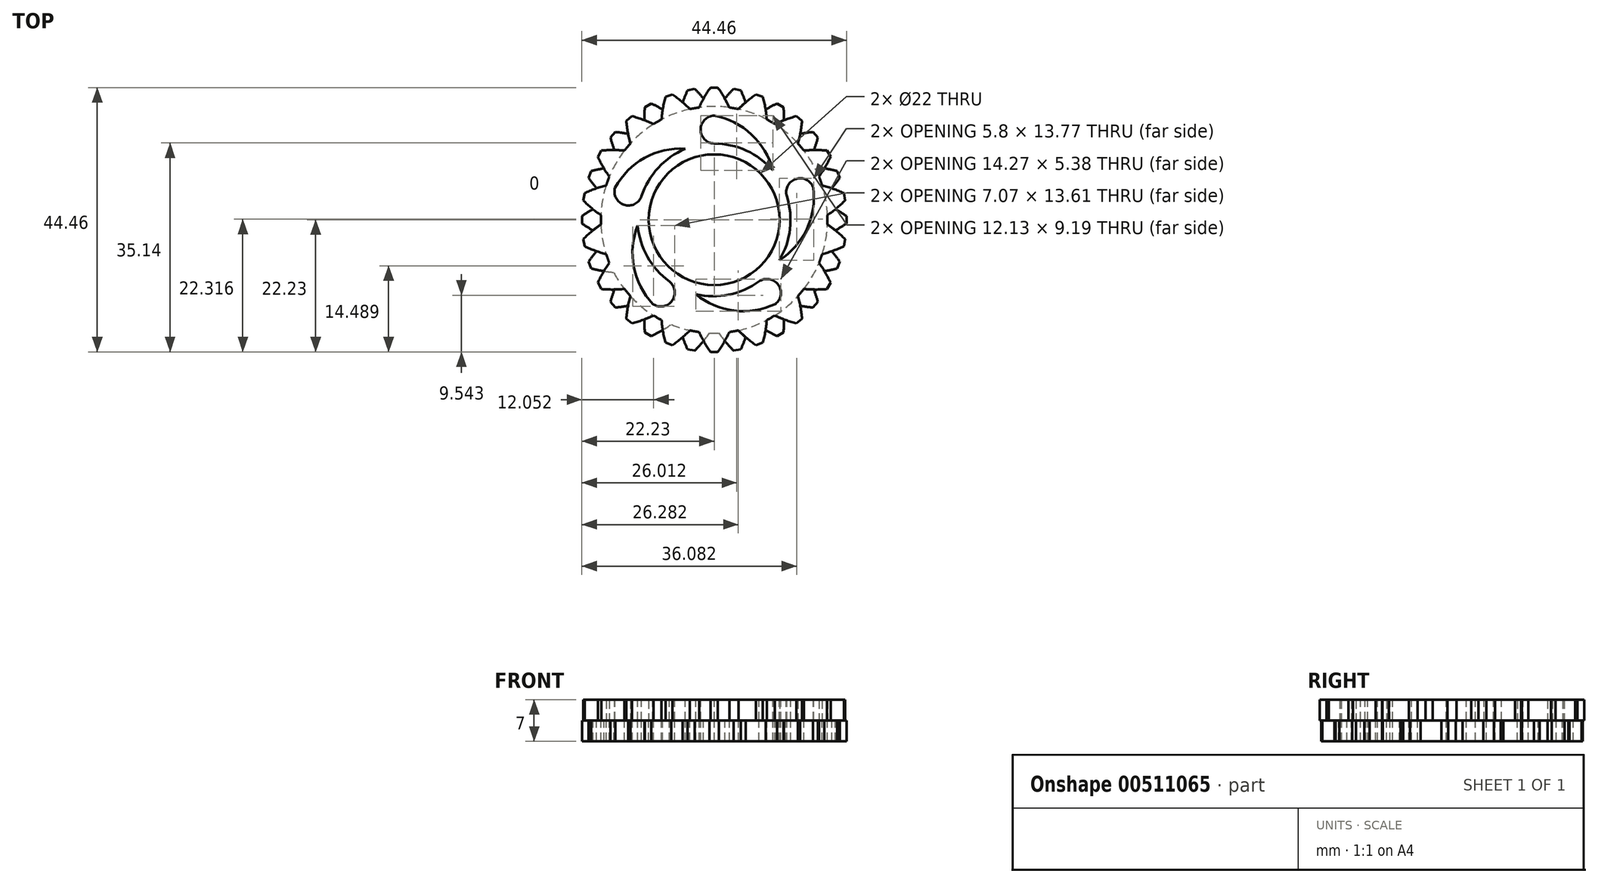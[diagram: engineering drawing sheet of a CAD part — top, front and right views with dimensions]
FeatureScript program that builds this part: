
annotation { "Feature Type Name" : "Feature", "Feature Type Description" : "" }
export const myFeature = defineFeature(function(context is Context, id is Id, definition is map)
    precondition{}
    {
        {
            var Q0;
            Q0=qCreatedBy(makeId("Top.planeOp"),FACE);
            var sketch = newSketch(context, id + "F0", { "sketchPlane" : qUnion([Q0])});
            skCircle(sketch, "E0", {"center": v(0, 0) * mm, "radius": 19.05 * mm});
            skCircle(sketch, "E1", {"center": v(0, 0) * mm, "radius": 11 * mm});
            skLineSegment(sketch, "E2", {"start": v(-2.54, 18.88) * mm, "end": v(-1, 22.23) * mm});
            skLineSegment(sketch, "E3", {"start": v(-1, 22.23) * mm, "end": v(1, 22.23) * mm});
            skLineSegment(sketch, "E4", {"start": v(1, 22.23) * mm, "end": v(2.54, 18.88) * mm});
            skArc(sketch, "E5", {"start": v(-0.62, 22.23) * mm, "mid": v(-1.65, 20.6) * mm, "end": v(-2.54, 18.88) * mm});
            skArc(sketch, "E6", {"start": v(2.54, 18.88) * mm, "mid": v(1.65, 20.6) * mm, "end": v(0.62, 22.23) * mm});
            skArc(sketch, "E7.1.0", {"start": v(-8.18, 20.67) * mm, "mid": v(-8.6, 18.79) * mm, "end": v(-8.84, 16.87) * mm});
            skLineSegment(sketch, "E7.1.1", {"start": v(-8.54, 20.54) * mm, "end": v(-6.66, 21.23) * mm});
            skArc(sketch, "E7.1.2", {"start": v(-4.07, 18.61) * mm, "mid": v(-5.49, 19.92) * mm, "end": v(-7.02, 21.1) * mm});
            skArc(sketch, "E7.2.0", {"start": v(-14.76, 16.63) * mm, "mid": v(-14.5, 14.71) * mm, "end": v(-14.08, 12.83) * mm});
            skLineSegment(sketch, "E7.2.1", {"start": v(-15.05, 16.38) * mm, "end": v(-13.52, 17.67) * mm});
            skArc(sketch, "E7.2.2", {"start": v(-10.2, 16.1) * mm, "mid": v(-11.97, 16.84) * mm, "end": v(-13.81, 17.42) * mm});
            skArc(sketch, "E7.3.0", {"start": v(-19.56, 10.58) * mm, "mid": v(-18.66, 8.86) * mm, "end": v(-17.62, 7.24) * mm});
            skLineSegment(sketch, "E7.3.1", {"start": v(-19.75, 10.25) * mm, "end": v(-18.75, 11.98) * mm});
            skArc(sketch, "E7.3.2", {"start": v(-15.08, 11.64) * mm, "mid": v(-17, 11.73) * mm, "end": v(-18.94, 11.65) * mm});
            skArc(sketch, "E7.4.0", {"start": v(-22, 3.25) * mm, "mid": v(-20.57, 1.95) * mm, "end": v(-19.03, 0.78) * mm});
            skLineSegment(sketch, "E7.4.1", {"start": v(-22.06, 2.87) * mm, "end": v(-21.71, 4.84) * mm});
            skArc(sketch, "E7.4.2", {"start": v(-18.15, 5.78) * mm, "mid": v(-20, 5.2) * mm, "end": v(-21.78, 4.47) * mm});
            skArc(sketch, "E7.5.0", {"start": v(-21.78, -4.47) * mm, "mid": v(-20, -5.2) * mm, "end": v(-18.15, -5.78) * mm});
            skLineSegment(sketch, "E7.5.1", {"start": v(-21.71, -4.84) * mm, "end": v(-22.06, -2.87) * mm});
            skArc(sketch, "E7.5.2", {"start": v(-19.03, -0.78) * mm, "mid": v(-20.57, -1.95) * mm, "end": v(-22, -3.25) * mm});
            skArc(sketch, "E7.6.0", {"start": v(-18.94, -11.65) * mm, "mid": v(-17, -11.73) * mm, "end": v(-15.08, -11.64) * mm});
            skLineSegment(sketch, "E7.6.1", {"start": v(-18.75, -11.98) * mm, "end": v(-19.75, -10.25) * mm});
            skArc(sketch, "E7.6.2", {"start": v(-17.62, -7.24) * mm, "mid": v(-18.66, -8.86) * mm, "end": v(-19.56, -10.58) * mm});
            skArc(sketch, "E7.7.0", {"start": v(-13.81, -17.42) * mm, "mid": v(-11.97, -16.84) * mm, "end": v(-10.2, -16.1) * mm});
            skLineSegment(sketch, "E7.7.1", {"start": v(-13.52, -17.67) * mm, "end": v(-15.05, -16.38) * mm});
            skArc(sketch, "E7.7.2", {"start": v(-14.08, -12.83) * mm, "mid": v(-14.5, -14.71) * mm, "end": v(-14.76, -16.63) * mm});
            skArc(sketch, "E7.8.0", {"start": v(-7.02, -21.1) * mm, "mid": v(-5.49, -19.92) * mm, "end": v(-4.07, -18.61) * mm});
            skLineSegment(sketch, "E7.8.1", {"start": v(-6.66, -21.23) * mm, "end": v(-8.54, -20.54) * mm});
            skArc(sketch, "E7.8.2", {"start": v(-8.84, -16.87) * mm, "mid": v(-8.6, -18.79) * mm, "end": v(-8.18, -20.67) * mm});
            skArc(sketch, "E7.9.0", {"start": v(0.62, -22.23) * mm, "mid": v(1.65, -20.6) * mm, "end": v(2.54, -18.88) * mm});
            skLineSegment(sketch, "E7.9.1", {"start": v(1, -22.23) * mm, "end": v(-1, -22.23) * mm});
            skArc(sketch, "E7.9.2", {"start": v(-2.54, -18.88) * mm, "mid": v(-1.65, -20.6) * mm, "end": v(-0.62, -22.23) * mm});
            skArc(sketch, "E7.10.0", {"start": v(8.18, -20.67) * mm, "mid": v(8.6, -18.79) * mm, "end": v(8.84, -16.87) * mm});
            skLineSegment(sketch, "E7.10.1", {"start": v(8.54, -20.54) * mm, "end": v(6.66, -21.23) * mm});
            skArc(sketch, "E7.10.2", {"start": v(4.07, -18.61) * mm, "mid": v(5.49, -19.92) * mm, "end": v(7.02, -21.1) * mm});
            skArc(sketch, "E7.11.0", {"start": v(14.76, -16.63) * mm, "mid": v(14.5, -14.71) * mm, "end": v(14.08, -12.83) * mm});
            skLineSegment(sketch, "E7.11.1", {"start": v(15.05, -16.38) * mm, "end": v(13.52, -17.67) * mm});
            skArc(sketch, "E7.11.2", {"start": v(10.2, -16.1) * mm, "mid": v(11.97, -16.84) * mm, "end": v(13.81, -17.42) * mm});
            skArc(sketch, "E7.12.0", {"start": v(19.56, -10.58) * mm, "mid": v(18.66, -8.86) * mm, "end": v(17.62, -7.24) * mm});
            skLineSegment(sketch, "E7.12.1", {"start": v(19.75, -10.25) * mm, "end": v(18.75, -11.98) * mm});
            skArc(sketch, "E7.12.2", {"start": v(15.08, -11.64) * mm, "mid": v(17, -11.73) * mm, "end": v(18.94, -11.65) * mm});
            skArc(sketch, "E7.13.0", {"start": v(22, -3.25) * mm, "mid": v(20.57, -1.95) * mm, "end": v(19.03, -0.78) * mm});
            skLineSegment(sketch, "E7.13.1", {"start": v(22.06, -2.87) * mm, "end": v(21.71, -4.84) * mm});
            skArc(sketch, "E7.13.2", {"start": v(18.15, -5.78) * mm, "mid": v(20, -5.2) * mm, "end": v(21.78, -4.47) * mm});
            skArc(sketch, "E7.14.0", {"start": v(21.78, 4.47) * mm, "mid": v(20, 5.2) * mm, "end": v(18.15, 5.78) * mm});
            skLineSegment(sketch, "E7.14.1", {"start": v(21.71, 4.84) * mm, "end": v(22.06, 2.87) * mm});
            skArc(sketch, "E7.14.2", {"start": v(19.03, 0.78) * mm, "mid": v(20.57, 1.95) * mm, "end": v(22, 3.25) * mm});
            skArc(sketch, "E7.15.0", {"start": v(18.94, 11.65) * mm, "mid": v(17, 11.73) * mm, "end": v(15.08, 11.64) * mm});
            skLineSegment(sketch, "E7.15.1", {"start": v(18.75, 11.98) * mm, "end": v(19.75, 10.25) * mm});
            skArc(sketch, "E7.15.2", {"start": v(17.62, 7.24) * mm, "mid": v(18.66, 8.86) * mm, "end": v(19.56, 10.58) * mm});
            skArc(sketch, "E7.16.0", {"start": v(13.81, 17.42) * mm, "mid": v(11.97, 16.84) * mm, "end": v(10.2, 16.1) * mm});
            skLineSegment(sketch, "E7.16.1", {"start": v(13.52, 17.67) * mm, "end": v(15.05, 16.38) * mm});
            skArc(sketch, "E7.16.2", {"start": v(14.08, 12.83) * mm, "mid": v(14.5, 14.71) * mm, "end": v(14.76, 16.63) * mm});
            skArc(sketch, "E7.17.0", {"start": v(7.02, 21.1) * mm, "mid": v(5.49, 19.92) * mm, "end": v(4.07, 18.61) * mm});
            skLineSegment(sketch, "E7.17.1", {"start": v(6.66, 21.23) * mm, "end": v(8.54, 20.54) * mm});
            skArc(sketch, "E7.17.2", {"start": v(8.84, 16.87) * mm, "mid": v(8.6, 18.79) * mm, "end": v(8.18, 20.67) * mm});
            skSolve(sketch);
        }
        {
            var Q0;
            {var subQ0=sQuery(id+"F0.wireOp",EDGE,"E7.1.0");Q0=makeQuery(id+"F0.imprint","IMPRINT",FACE,{"disambiguationData":[TD([[makeQuery(id+"F0.imprint","IMPRINT",EDGE,{"derivedFrom":subQ0}),1.0]])]});}
            var Q1;
            Q1=makeQuery(id+"F0.imprint","IMPRINT",FACE,{"disambiguationData":[TD([[makeQuery(id+"F0.imprint","IMPRINT",EDGE,{"derivedFrom":sQuery(id+"F0.wireOp",EDGE,"E1")}),-1.0]])]});
            var Q2;
            {var subQ0=sQuery(id+"F0.wireOp",EDGE,"E5");Q2=makeQuery(id+"F0.imprint","IMPRINT",FACE,{"disambiguationData":[TD([[makeQuery(id+"F0.imprint","IMPRINT",EDGE,{"derivedFrom":subQ0}),1.0]])]});}
            var Q3;
            {var subQ0=sQuery(id+"F0.wireOp",EDGE,"E7.17.0");Q3=makeQuery(id+"F0.imprint","IMPRINT",FACE,{"disambiguationData":[TD([[makeQuery(id+"F0.imprint","IMPRINT",EDGE,{"derivedFrom":subQ0}),1.0]])]});}
            var Q4;
            {var subQ0=sQuery(id+"F0.wireOp",EDGE,"E7.16.0");Q4=makeQuery(id+"F0.imprint","IMPRINT",FACE,{"disambiguationData":[TD([[makeQuery(id+"F0.imprint","IMPRINT",EDGE,{"derivedFrom":subQ0}),1.0]])]});}
            var Q5;
            {var subQ0=sQuery(id+"F0.wireOp",EDGE,"E7.15.0");Q5=makeQuery(id+"F0.imprint","IMPRINT",FACE,{"disambiguationData":[TD([[makeQuery(id+"F0.imprint","IMPRINT",EDGE,{"derivedFrom":subQ0}),1.0]])]});}
            var Q6;
            {var subQ0=sQuery(id+"F0.wireOp",EDGE,"E7.14.0");Q6=makeQuery(id+"F0.imprint","IMPRINT",FACE,{"disambiguationData":[TD([[makeQuery(id+"F0.imprint","IMPRINT",EDGE,{"derivedFrom":subQ0}),1.0]])]});}
            var Q7;
            {var subQ0=sQuery(id+"F0.wireOp",EDGE,"E7.13.0");Q7=makeQuery(id+"F0.imprint","IMPRINT",FACE,{"disambiguationData":[TD([[makeQuery(id+"F0.imprint","IMPRINT",EDGE,{"derivedFrom":subQ0}),1.0]])]});}
            var Q8;
            {var subQ0=sQuery(id+"F0.wireOp",EDGE,"E7.12.0");Q8=makeQuery(id+"F0.imprint","IMPRINT",FACE,{"disambiguationData":[TD([[makeQuery(id+"F0.imprint","IMPRINT",EDGE,{"derivedFrom":subQ0}),1.0]])]});}
            var Q9;
            {var subQ0=sQuery(id+"F0.wireOp",EDGE,"E7.11.0");Q9=makeQuery(id+"F0.imprint","IMPRINT",FACE,{"disambiguationData":[TD([[makeQuery(id+"F0.imprint","IMPRINT",EDGE,{"derivedFrom":subQ0}),1.0]])]});}
            var Q10;
            {var subQ0=sQuery(id+"F0.wireOp",EDGE,"E7.10.0");Q10=makeQuery(id+"F0.imprint","IMPRINT",FACE,{"disambiguationData":[TD([[makeQuery(id+"F0.imprint","IMPRINT",EDGE,{"derivedFrom":subQ0}),1.0]])]});}
            var Q11;
            {var subQ0=sQuery(id+"F0.wireOp",EDGE,"E7.9.0");Q11=makeQuery(id+"F0.imprint","IMPRINT",FACE,{"disambiguationData":[TD([[makeQuery(id+"F0.imprint","IMPRINT",EDGE,{"derivedFrom":subQ0}),1.0]])]});}
            var Q12;
            {var subQ0=sQuery(id+"F0.wireOp",EDGE,"E7.8.0");Q12=makeQuery(id+"F0.imprint","IMPRINT",FACE,{"disambiguationData":[TD([[makeQuery(id+"F0.imprint","IMPRINT",EDGE,{"derivedFrom":subQ0}),1.0]])]});}
            var Q13;
            {var subQ0=sQuery(id+"F0.wireOp",EDGE,"E7.7.0");Q13=makeQuery(id+"F0.imprint","IMPRINT",FACE,{"disambiguationData":[TD([[makeQuery(id+"F0.imprint","IMPRINT",EDGE,{"derivedFrom":subQ0}),1.0]])]});}
            var Q14;
            {var subQ0=sQuery(id+"F0.wireOp",EDGE,"E7.6.0");Q14=makeQuery(id+"F0.imprint","IMPRINT",FACE,{"disambiguationData":[TD([[makeQuery(id+"F0.imprint","IMPRINT",EDGE,{"derivedFrom":subQ0}),1.0]])]});}
            var Q15;
            {var subQ0=sQuery(id+"F0.wireOp",EDGE,"E7.5.0");Q15=makeQuery(id+"F0.imprint","IMPRINT",FACE,{"disambiguationData":[TD([[makeQuery(id+"F0.imprint","IMPRINT",EDGE,{"derivedFrom":subQ0}),1.0]])]});}
            var Q16;
            {var subQ0=sQuery(id+"F0.wireOp",EDGE,"E7.4.0");Q16=makeQuery(id+"F0.imprint","IMPRINT",FACE,{"disambiguationData":[TD([[makeQuery(id+"F0.imprint","IMPRINT",EDGE,{"derivedFrom":subQ0}),1.0]])]});}
            var Q17;
            {var subQ0=sQuery(id+"F0.wireOp",EDGE,"E7.3.0");Q17=makeQuery(id+"F0.imprint","IMPRINT",FACE,{"disambiguationData":[TD([[makeQuery(id+"F0.imprint","IMPRINT",EDGE,{"derivedFrom":subQ0}),1.0]])]});}
            var Q18;
            {var subQ0=sQuery(id+"F0.wireOp",EDGE,"E7.2.0");Q18=makeQuery(id+"F0.imprint","IMPRINT",FACE,{"disambiguationData":[TD([[makeQuery(id+"F0.imprint","IMPRINT",EDGE,{"derivedFrom":subQ0}),1.0]])]});}
            extrude(context, id + "F1", {"entities" : qUnion([Q0, Q1, Q2, Q3, Q4, Q5, Q6, Q7, Q8, Q9, Q10, Q11, Q12, Q13, Q14, Q15, Q16, Q17, Q18]), "depth" : 3.5 * mm, "offsetDistance" : 25.4 * mm});
        }
        {
            var Q0;
            Q0=makeQuery(id+"F1.opExtrude","CAP_FACE",FACE,{"disambiguationData":[OSD([sQuery(id+"F0.wireOp",EDGE,"E0"),sQuery(id+"F0.wireOp",EDGE,"E1"),sQuery(id+"F0.wireOp",EDGE,"E3"),sQuery(id+"F0.wireOp",EDGE,"E5"),sQuery(id+"F0.wireOp",EDGE,"E6"),sQuery(id+"F0.wireOp",EDGE,"E7.1.0"),sQuery(id+"F0.wireOp",EDGE,"E7.1.1"),sQuery(id+"F0.wireOp",EDGE,"E7.1.2"),sQuery(id+"F0.wireOp",EDGE,"E7.2.0"),sQuery(id+"F0.wireOp",EDGE,"E7.2.1"),sQuery(id+"F0.wireOp",EDGE,"E7.2.2"),sQuery(id+"F0.wireOp",EDGE,"E7.3.0"),sQuery(id+"F0.wireOp",EDGE,"E7.3.1"),sQuery(id+"F0.wireOp",EDGE,"E7.3.2"),sQuery(id+"F0.wireOp",EDGE,"E7.4.0"),sQuery(id+"F0.wireOp",EDGE,"E7.4.1"),sQuery(id+"F0.wireOp",EDGE,"E7.4.2"),sQuery(id+"F0.wireOp",EDGE,"E7.5.0"),sQuery(id+"F0.wireOp",EDGE,"E7.5.1"),sQuery(id+"F0.wireOp",EDGE,"E7.5.2"),sQuery(id+"F0.wireOp",EDGE,"E7.6.0"),sQuery(id+"F0.wireOp",EDGE,"E7.6.1"),sQuery(id+"F0.wireOp",EDGE,"E7.6.2"),sQuery(id+"F0.wireOp",EDGE,"E7.7.0"),sQuery(id+"F0.wireOp",EDGE,"E7.7.1"),sQuery(id+"F0.wireOp",EDGE,"E7.7.2"),sQuery(id+"F0.wireOp",EDGE,"E7.8.0"),sQuery(id+"F0.wireOp",EDGE,"E7.8.1"),sQuery(id+"F0.wireOp",EDGE,"E7.8.2"),sQuery(id+"F0.wireOp",EDGE,"E7.9.0"),sQuery(id+"F0.wireOp",EDGE,"E7.9.1"),sQuery(id+"F0.wireOp",EDGE,"E7.9.2"),sQuery(id+"F0.wireOp",EDGE,"E7.10.0"),sQuery(id+"F0.wireOp",EDGE,"E7.10.1"),sQuery(id+"F0.wireOp",EDGE,"E7.10.2"),sQuery(id+"F0.wireOp",EDGE,"E7.11.0"),sQuery(id+"F0.wireOp",EDGE,"E7.11.1"),sQuery(id+"F0.wireOp",EDGE,"E7.11.2"),sQuery(id+"F0.wireOp",EDGE,"E7.12.0"),sQuery(id+"F0.wireOp",EDGE,"E7.12.1"),sQuery(id+"F0.wireOp",EDGE,"E7.12.2"),sQuery(id+"F0.wireOp",EDGE,"E7.13.0"),sQuery(id+"F0.wireOp",EDGE,"E7.13.1"),sQuery(id+"F0.wireOp",EDGE,"E7.13.2"),sQuery(id+"F0.wireOp",EDGE,"E7.14.0"),sQuery(id+"F0.wireOp",EDGE,"E7.14.1"),sQuery(id+"F0.wireOp",EDGE,"E7.14.2"),sQuery(id+"F0.wireOp",EDGE,"E7.15.0"),sQuery(id+"F0.wireOp",EDGE,"E7.15.1"),sQuery(id+"F0.wireOp",EDGE,"E7.15.2"),sQuery(id+"F0.wireOp",EDGE,"E7.16.0"),sQuery(id+"F0.wireOp",EDGE,"E7.16.1"),sQuery(id+"F0.wireOp",EDGE,"E7.16.2"),sQuery(id+"F0.wireOp",EDGE,"E7.17.0"),sQuery(id+"F0.wireOp",EDGE,"E7.17.1"),sQuery(id+"F0.wireOp",EDGE,"E7.17.2")])],"isStart":true});
            var sketch = newSketch(context, id + "F2", { "sketchPlane" : qUnion([Q0])});
            skCircle(sketch, "E8.0", {"center": v(0, 0) * mm, "radius": 11 * mm});
            skArc(sketch, "E9.0", {"start": v(-2.54, 18.88) * mm, "mid": v(-1.65, 20.6) * mm, "end": v(-0.62, 22.23) * mm});
            skLineSegment(sketch, "E10.0", {"start": v(0.62, 22.23) * mm, "end": v(-0.62, 22.23) * mm});
            skArc(sketch, "E11.0", {"start": v(0.62, 22.23) * mm, "mid": v(1.65, 20.6) * mm, "end": v(2.54, 18.88) * mm});
            skArc(sketch, "E12.1.0", {"start": v(-5.78, 18.15) * mm, "mid": v(-5.2, 20) * mm, "end": v(-4.47, 21.78) * mm});
            skLineSegment(sketch, "E12.1.1", {"start": v(-3.25, 22) * mm, "end": v(-4.47, 21.78) * mm});
            skArc(sketch, "E12.1.2", {"start": v(-3.25, 22) * mm, "mid": v(-1.95, 20.57) * mm, "end": v(-0.78, 19.03) * mm});
            skArc(sketch, "E12.2.0", {"start": v(-8.84, 16.87) * mm, "mid": v(-8.6, 18.79) * mm, "end": v(-8.18, 20.67) * mm});
            skArc(sketch, "E12.3.0", {"start": v(-11.64, 15.08) * mm, "mid": v(-11.73, 17) * mm, "end": v(-11.65, 18.94) * mm});
            skLineSegment(sketch, "E12.3.1", {"start": v(-10.58, 19.56) * mm, "end": v(-11.65, 18.94) * mm});
            skArc(sketch, "E12.3.2", {"start": v(-10.58, 19.56) * mm, "mid": v(-8.86, 18.66) * mm, "end": v(-7.24, 17.62) * mm});
            skArc(sketch, "E12.5.0", {"start": v(-16.1, 10.2) * mm, "mid": v(-16.84, 11.97) * mm, "end": v(-17.42, 13.81) * mm});
            skLineSegment(sketch, "E12.5.1", {"start": v(-16.63, 14.76) * mm, "end": v(-17.42, 13.81) * mm});
            skArc(sketch, "E12.5.2", {"start": v(-16.63, 14.76) * mm, "mid": v(-14.71, 14.5) * mm, "end": v(-12.83, 14.08) * mm});
            skArc(sketch, "E12.6.0", {"start": v(-17.62, 7.24) * mm, "mid": v(-18.66, 8.86) * mm, "end": v(-19.56, 10.58) * mm});
            skLineSegment(sketch, "E12.6.1", {"start": v(-18.94, 11.65) * mm, "end": v(-19.56, 10.58) * mm});
            skArc(sketch, "E12.6.2", {"start": v(-18.94, 11.65) * mm, "mid": v(-17, 11.73) * mm, "end": v(-15.08, 11.64) * mm});
            skArc(sketch, "E12.7.0", {"start": v(-18.61, 4.07) * mm, "mid": v(-19.92, 5.49) * mm, "end": v(-21.1, 7.02) * mm});
            skLineSegment(sketch, "E12.7.1", {"start": v(-20.67, 8.18) * mm, "end": v(-21.1, 7.02) * mm});
            skArc(sketch, "E12.7.2", {"start": v(-20.67, 8.18) * mm, "mid": v(-18.79, 8.6) * mm, "end": v(-16.87, 8.84) * mm});
            skArc(sketch, "E12.9.0", {"start": v(-18.88, -2.54) * mm, "mid": v(-20.6, -1.65) * mm, "end": v(-22.23, -0.62) * mm});
            skLineSegment(sketch, "E12.9.1", {"start": v(-22.23, 0.62) * mm, "end": v(-22.23, -0.62) * mm});
            skArc(sketch, "E12.9.2", {"start": v(-22.22, 0.62) * mm, "mid": v(-20.6, 1.65) * mm, "end": v(-18.88, 2.54) * mm});
            skArc(sketch, "E12.11.0", {"start": v(-16.87, -8.84) * mm, "mid": v(-18.79, -8.6) * mm, "end": v(-20.67, -8.18) * mm});
            skLineSegment(sketch, "E12.11.1", {"start": v(-21.1, -7.02) * mm, "end": v(-20.67, -8.18) * mm});
            skArc(sketch, "E12.11.2", {"start": v(-21.1, -7.02) * mm, "mid": v(-19.92, -5.49) * mm, "end": v(-18.61, -4.07) * mm});
            skArc(sketch, "E12.13.0", {"start": v(-12.83, -14.08) * mm, "mid": v(-14.71, -14.5) * mm, "end": v(-16.63, -14.76) * mm});
            skLineSegment(sketch, "E12.13.1", {"start": v(-17.42, -13.81) * mm, "end": v(-16.63, -14.76) * mm});
            skArc(sketch, "E12.13.2", {"start": v(-17.42, -13.81) * mm, "mid": v(-16.84, -11.97) * mm, "end": v(-16.1, -10.2) * mm});
            skArc(sketch, "E12.15.0", {"start": v(-7.24, -17.62) * mm, "mid": v(-8.86, -18.66) * mm, "end": v(-10.58, -19.56) * mm});
            skLineSegment(sketch, "E12.15.1", {"start": v(-11.65, -18.94) * mm, "end": v(-10.58, -19.56) * mm});
            skArc(sketch, "E12.15.2", {"start": v(-11.65, -18.94) * mm, "mid": v(-11.73, -17) * mm, "end": v(-11.64, -15.08) * mm});
            skArc(sketch, "E12.17.0", {"start": v(-0.78, -19.03) * mm, "mid": v(-1.95, -20.57) * mm, "end": v(-3.25, -22) * mm});
            skLineSegment(sketch, "E12.17.1", {"start": v(-4.47, -21.78) * mm, "end": v(-3.25, -22) * mm});
            skArc(sketch, "E12.17.2", {"start": v(-4.47, -21.78) * mm, "mid": v(-5.2, -20) * mm, "end": v(-5.78, -18.15) * mm});
            skArc(sketch, "E12.19.0", {"start": v(5.78, -18.15) * mm, "mid": v(5.2, -20) * mm, "end": v(4.47, -21.78) * mm});
            skLineSegment(sketch, "E12.19.1", {"start": v(3.25, -22) * mm, "end": v(4.47, -21.78) * mm});
            skArc(sketch, "E12.19.2", {"start": v(3.25, -22) * mm, "mid": v(1.95, -20.57) * mm, "end": v(0.78, -19.03) * mm});
            skArc(sketch, "E12.21.0", {"start": v(11.64, -15.08) * mm, "mid": v(11.73, -17) * mm, "end": v(11.65, -18.94) * mm});
            skLineSegment(sketch, "E12.21.1", {"start": v(10.58, -19.56) * mm, "end": v(11.65, -18.94) * mm});
            skArc(sketch, "E12.21.2", {"start": v(10.58, -19.56) * mm, "mid": v(8.86, -18.66) * mm, "end": v(7.24, -17.62) * mm});
            skArc(sketch, "E12.23.0", {"start": v(16.1, -10.2) * mm, "mid": v(16.84, -11.97) * mm, "end": v(17.42, -13.81) * mm});
            skLineSegment(sketch, "E12.23.1", {"start": v(16.63, -14.76) * mm, "end": v(17.42, -13.81) * mm});
            skArc(sketch, "E12.23.2", {"start": v(16.63, -14.76) * mm, "mid": v(14.71, -14.5) * mm, "end": v(12.83, -14.08) * mm});
            skArc(sketch, "E12.25.0", {"start": v(18.61, -4.07) * mm, "mid": v(19.92, -5.49) * mm, "end": v(21.1, -7.02) * mm});
            skLineSegment(sketch, "E12.25.1", {"start": v(20.67, -8.18) * mm, "end": v(21.1, -7.02) * mm});
            skArc(sketch, "E12.25.2", {"start": v(20.67, -8.18) * mm, "mid": v(18.79, -8.6) * mm, "end": v(16.87, -8.84) * mm});
            skArc(sketch, "E12.27.0", {"start": v(18.88, 2.54) * mm, "mid": v(20.6, 1.65) * mm, "end": v(22.23, 0.62) * mm});
            skLineSegment(sketch, "E12.27.1", {"start": v(22.23, -0.62) * mm, "end": v(22.23, 0.62) * mm});
            skArc(sketch, "E12.27.2", {"start": v(22.22, -0.62) * mm, "mid": v(20.6, -1.65) * mm, "end": v(18.88, -2.54) * mm});
            skArc(sketch, "E12.29.0", {"start": v(16.87, 8.84) * mm, "mid": v(18.79, 8.6) * mm, "end": v(20.67, 8.18) * mm});
            skLineSegment(sketch, "E12.29.1", {"start": v(21.1, 7.02) * mm, "end": v(20.67, 8.18) * mm});
            skArc(sketch, "E12.29.2", {"start": v(21.1, 7.02) * mm, "mid": v(19.92, 5.49) * mm, "end": v(18.61, 4.07) * mm});
            skArc(sketch, "E12.31.0", {"start": v(12.83, 14.08) * mm, "mid": v(14.71, 14.5) * mm, "end": v(16.63, 14.76) * mm});
            skLineSegment(sketch, "E12.31.1", {"start": v(17.42, 13.81) * mm, "end": v(16.63, 14.76) * mm});
            skArc(sketch, "E12.31.2", {"start": v(17.42, 13.81) * mm, "mid": v(16.84, 11.97) * mm, "end": v(16.1, 10.2) * mm});
            skArc(sketch, "E12.33.0", {"start": v(7.24, 17.62) * mm, "mid": v(8.86, 18.66) * mm, "end": v(10.58, 19.56) * mm});
            skLineSegment(sketch, "E12.33.1", {"start": v(11.65, 18.94) * mm, "end": v(10.58, 19.56) * mm});
            skArc(sketch, "E12.33.2", {"start": v(11.65, 18.94) * mm, "mid": v(11.73, 17) * mm, "end": v(11.64, 15.08) * mm});
            skArc(sketch, "E12.35.0", {"start": v(0.78, 19.03) * mm, "mid": v(1.95, 20.57) * mm, "end": v(3.25, 22) * mm});
            skLineSegment(sketch, "E12.35.1", {"start": v(4.47, 21.78) * mm, "end": v(3.25, 22) * mm});
            skArc(sketch, "E12.35.2", {"start": v(4.47, 21.78) * mm, "mid": v(5.2, 20) * mm, "end": v(5.78, 18.15) * mm});
            skCircle(sketch, "E13", {"center": v(0, 0) * mm, "radius": 19.05 * mm});
            skSolve(sketch);
        }
        {
            var Q0;
            Q0=makeQuery(id+"F2.imprint","IMPRINT",FACE,{"disambiguationData":[TD([[makeQuery(id+"F2.imprint","IMPRINT",EDGE,{"derivedFrom":sQuery(id+"F2.wireOp",EDGE,"E8.0")}),1.0]])]});
            var Q1;
            {var subQ0=sQuery(id+"F2.wireOp",EDGE,"E12.3.1");Q1=makeQuery(id+"F2.imprint","IMPRINT",FACE,{"disambiguationData":[TD([[makeQuery(id+"F2.imprint","IMPRINT",EDGE,{"derivedFrom":subQ0}),1.0]])]});}
            var Q2;
            {var subQ0=sQuery(id+"F2.wireOp",EDGE,"E13");var subQ1=sQuery(id+"F2.wireOp",EDGE,"E12.2.0");var subQ2=makeQuery(id+"F2.imprint","INTERSECT",VERTEX,{"derivedFrom":[subQ1,subQ0]});Q2=makeQuery(id+"F2.imprint","IMPRINT",FACE,{"disambiguationData":[TD([[makeQuery(id+"F2.imprint","IMPRINT",EDGE,{"disambiguationData":[TD([[subQ2,-1.0]])],"derivedFrom":subQ1}),-1.0]])]});}
            var Q3;
            {var subQ0=sQuery(id+"F2.wireOp",EDGE,"E13");var subQ1=sQuery(id+"F2.wireOp",EDGE,"E12.3.0");var subQ2=makeQuery(id+"F2.imprint","INTERSECT",VERTEX,{"derivedFrom":[subQ1,subQ0]});Q3=makeQuery(id+"F2.imprint","IMPRINT",FACE,{"disambiguationData":[TD([[makeQuery(id+"F2.imprint","IMPRINT",EDGE,{"disambiguationData":[TD([[subQ2,-1.0]])],"derivedFrom":subQ1}),-1.0]])]});}
            var Q4;
            {var subQ0=sQuery(id+"F2.wireOp",EDGE,"E13");var subQ1=sQuery(id+"F2.wireOp",EDGE,"E12.1.0");var subQ2=makeQuery(id+"F2.imprint","INTERSECT",VERTEX,{"derivedFrom":[subQ1,subQ0]});Q4=makeQuery(id+"F2.imprint","IMPRINT",FACE,{"disambiguationData":[TD([[makeQuery(id+"F2.imprint","IMPRINT",EDGE,{"disambiguationData":[TD([[subQ2,-1.0]])],"derivedFrom":subQ1}),-1.0]])]});}
            var Q5;
            {var subQ1=sQuery(id+"F2.wireOp",EDGE,"E12.1.1");Q5=makeQuery(id+"F2.imprint","IMPRINT",FACE,{"disambiguationData":[TD([[makeQuery(id+"F2.imprint","IMPRINT",EDGE,{"derivedFrom":subQ1}),1.0]])]});}
            var Q6;
            {var subQ0=sQuery(id+"F2.wireOp",EDGE,"E13");var subQ1=sQuery(id+"F2.wireOp",EDGE,"E9.0");var subQ2=makeQuery(id+"F2.imprint","INTERSECT",VERTEX,{"derivedFrom":[subQ1,subQ0]});Q6=makeQuery(id+"F2.imprint","IMPRINT",FACE,{"disambiguationData":[TD([[makeQuery(id+"F2.imprint","IMPRINT",EDGE,{"disambiguationData":[TD([[subQ2,-1.0]])],"derivedFrom":subQ1}),-1.0]])]});}
            var Q7;
            {var subQ0=sQuery(id+"F2.wireOp",EDGE,"E13");var subQ1=sQuery(id+"F2.wireOp",EDGE,"E11.0");var subQ2=makeQuery(id+"F2.imprint","INTERSECT",VERTEX,{"derivedFrom":[subQ1,subQ0]});Q7=makeQuery(id+"F2.imprint","IMPRINT",FACE,{"disambiguationData":[TD([[makeQuery(id+"F2.imprint","IMPRINT",EDGE,{"disambiguationData":[TD([[subQ2,1.0]])],"derivedFrom":subQ1}),-1.0]])]});}
            var Q8;
            {var subQ1=sQuery(id+"F2.wireOp",EDGE,"E12.35.1");Q8=makeQuery(id+"F2.imprint","IMPRINT",FACE,{"disambiguationData":[TD([[makeQuery(id+"F2.imprint","IMPRINT",EDGE,{"derivedFrom":subQ1}),1.0]])]});}
            var Q9;
            {var subQ0=sQuery(id+"F2.wireOp",EDGE,"E13");var subQ1=sQuery(id+"F2.wireOp",EDGE,"E12.35.2");var subQ2=makeQuery(id+"F2.imprint","INTERSECT",VERTEX,{"derivedFrom":[subQ1,subQ0]});Q9=makeQuery(id+"F2.imprint","IMPRINT",FACE,{"disambiguationData":[TD([[makeQuery(id+"F2.imprint","IMPRINT",EDGE,{"disambiguationData":[TD([[subQ2,1.0]])],"derivedFrom":subQ1}),-1.0]])]});}
            var Q10;
            {var subQ0=sQuery(id+"F2.wireOp",EDGE,"E13");var subQ1=sQuery(id+"F2.wireOp",EDGE,"E12.33.0");var subQ2=makeQuery(id+"F2.imprint","INTERSECT",VERTEX,{"derivedFrom":[subQ1,subQ0]});Q10=makeQuery(id+"F2.imprint","IMPRINT",FACE,{"disambiguationData":[TD([[makeQuery(id+"F2.imprint","IMPRINT",EDGE,{"disambiguationData":[TD([[subQ2,-1.0]])],"derivedFrom":subQ1}),-1.0]])]});}
            var Q11;
            {var subQ6=sQuery(id+"F2.wireOp",EDGE,"E12.33.1");Q11=makeQuery(id+"F2.imprint","IMPRINT",FACE,{"disambiguationData":[TD([[makeQuery(id+"F2.imprint","IMPRINT",EDGE,{"derivedFrom":subQ6}),1.0]])]});}
            var Q12;
            {var subQ0=sQuery(id+"F2.wireOp",EDGE,"E13");var subQ1=sQuery(id+"F2.wireOp",EDGE,"E12.33.2");var subQ2=makeQuery(id+"F2.imprint","INTERSECT",VERTEX,{"derivedFrom":[subQ1,subQ0]});Q12=makeQuery(id+"F2.imprint","IMPRINT",FACE,{"disambiguationData":[TD([[makeQuery(id+"F2.imprint","IMPRINT",EDGE,{"disambiguationData":[TD([[subQ2,1.0]])],"derivedFrom":subQ1}),-1.0]])]});}
            var Q13;
            {var subQ0=sQuery(id+"F2.wireOp",EDGE,"E13");var subQ1=sQuery(id+"F2.wireOp",EDGE,"E12.31.0");var subQ2=makeQuery(id+"F2.imprint","INTERSECT",VERTEX,{"derivedFrom":[subQ1,subQ0]});Q13=makeQuery(id+"F2.imprint","IMPRINT",FACE,{"disambiguationData":[TD([[makeQuery(id+"F2.imprint","IMPRINT",EDGE,{"disambiguationData":[TD([[subQ2,-1.0]])],"derivedFrom":subQ1}),-1.0]])]});}
            var Q14;
            {var subQ5=sQuery(id+"F2.wireOp",EDGE,"E12.31.1");Q14=makeQuery(id+"F2.imprint","IMPRINT",FACE,{"disambiguationData":[TD([[makeQuery(id+"F2.imprint","IMPRINT",EDGE,{"derivedFrom":subQ5}),1.0]])]});}
            var Q15;
            {var subQ0=sQuery(id+"F2.wireOp",EDGE,"E13");var subQ1=sQuery(id+"F2.wireOp",EDGE,"E12.31.2");var subQ2=makeQuery(id+"F2.imprint","INTERSECT",VERTEX,{"derivedFrom":[subQ1,subQ0]});Q15=makeQuery(id+"F2.imprint","IMPRINT",FACE,{"disambiguationData":[TD([[makeQuery(id+"F2.imprint","IMPRINT",EDGE,{"disambiguationData":[TD([[subQ2,1.0]])],"derivedFrom":subQ1}),-1.0]])]});}
            var Q16;
            {var subQ0=sQuery(id+"F2.wireOp",EDGE,"E13");var subQ1=sQuery(id+"F2.wireOp",EDGE,"E12.29.0");var subQ2=makeQuery(id+"F2.imprint","INTERSECT",VERTEX,{"derivedFrom":[subQ1,subQ0]});Q16=makeQuery(id+"F2.imprint","IMPRINT",FACE,{"disambiguationData":[TD([[makeQuery(id+"F2.imprint","IMPRINT",EDGE,{"disambiguationData":[TD([[subQ2,-1.0]])],"derivedFrom":subQ1}),-1.0]])]});}
            var Q17;
            {var subQ1=sQuery(id+"F2.wireOp",EDGE,"E12.29.1");Q17=makeQuery(id+"F2.imprint","IMPRINT",FACE,{"disambiguationData":[TD([[makeQuery(id+"F2.imprint","IMPRINT",EDGE,{"derivedFrom":subQ1}),1.0]])]});}
            var Q18;
            {var subQ0=sQuery(id+"F2.wireOp",EDGE,"E13");var subQ1=sQuery(id+"F2.wireOp",EDGE,"E12.29.2");var subQ2=makeQuery(id+"F2.imprint","INTERSECT",VERTEX,{"derivedFrom":[subQ1,subQ0]});Q18=makeQuery(id+"F2.imprint","IMPRINT",FACE,{"disambiguationData":[TD([[makeQuery(id+"F2.imprint","IMPRINT",EDGE,{"disambiguationData":[TD([[subQ2,1.0]])],"derivedFrom":subQ1}),-1.0]])]});}
            var Q19;
            {var subQ0=sQuery(id+"F2.wireOp",EDGE,"E13");var subQ1=sQuery(id+"F2.wireOp",EDGE,"E12.27.0");var subQ2=makeQuery(id+"F2.imprint","INTERSECT",VERTEX,{"derivedFrom":[subQ1,subQ0]});Q19=makeQuery(id+"F2.imprint","IMPRINT",FACE,{"disambiguationData":[TD([[makeQuery(id+"F2.imprint","IMPRINT",EDGE,{"disambiguationData":[TD([[subQ2,-1.0]])],"derivedFrom":subQ1}),-1.0]])]});}
            var Q20;
            {var subQ1=sQuery(id+"F2.wireOp",EDGE,"E12.27.1");Q20=makeQuery(id+"F2.imprint","IMPRINT",FACE,{"disambiguationData":[TD([[makeQuery(id+"F2.imprint","IMPRINT",EDGE,{"derivedFrom":subQ1}),1.0]])]});}
            var Q21;
            {var subQ0=sQuery(id+"F2.wireOp",EDGE,"E13");var subQ1=sQuery(id+"F2.wireOp",EDGE,"E12.27.2");var subQ2=makeQuery(id+"F2.imprint","INTERSECT",VERTEX,{"derivedFrom":[subQ1,subQ0]});Q21=makeQuery(id+"F2.imprint","IMPRINT",FACE,{"disambiguationData":[TD([[makeQuery(id+"F2.imprint","IMPRINT",EDGE,{"disambiguationData":[TD([[subQ2,1.0]])],"derivedFrom":subQ1}),-1.0]])]});}
            var Q22;
            {var subQ0=sQuery(id+"F2.wireOp",EDGE,"E13");var subQ1=sQuery(id+"F2.wireOp",EDGE,"E12.25.0");var subQ2=makeQuery(id+"F2.imprint","INTERSECT",VERTEX,{"derivedFrom":[subQ1,subQ0]});Q22=makeQuery(id+"F2.imprint","IMPRINT",FACE,{"disambiguationData":[TD([[makeQuery(id+"F2.imprint","IMPRINT",EDGE,{"disambiguationData":[TD([[subQ2,-1.0]])],"derivedFrom":subQ1}),-1.0]])]});}
            var Q23;
            {var subQ8=sQuery(id+"F2.wireOp",EDGE,"E12.25.1");Q23=makeQuery(id+"F2.imprint","IMPRINT",FACE,{"disambiguationData":[TD([[makeQuery(id+"F2.imprint","IMPRINT",EDGE,{"derivedFrom":subQ8}),1.0]])]});}
            var Q24;
            {var subQ0=sQuery(id+"F2.wireOp",EDGE,"E13");var subQ1=sQuery(id+"F2.wireOp",EDGE,"E12.25.2");var subQ2=makeQuery(id+"F2.imprint","INTERSECT",VERTEX,{"derivedFrom":[subQ1,subQ0]});Q24=makeQuery(id+"F2.imprint","IMPRINT",FACE,{"disambiguationData":[TD([[makeQuery(id+"F2.imprint","IMPRINT",EDGE,{"disambiguationData":[TD([[subQ2,1.0]])],"derivedFrom":subQ1}),-1.0]])]});}
            var Q25;
            {var subQ0=sQuery(id+"F2.wireOp",EDGE,"E13");var subQ1=sQuery(id+"F2.wireOp",EDGE,"E12.23.0");var subQ2=makeQuery(id+"F2.imprint","INTERSECT",VERTEX,{"derivedFrom":[subQ1,subQ0]});Q25=makeQuery(id+"F2.imprint","IMPRINT",FACE,{"disambiguationData":[TD([[makeQuery(id+"F2.imprint","IMPRINT",EDGE,{"disambiguationData":[TD([[subQ2,-1.0]])],"derivedFrom":subQ1}),-1.0]])]});}
            var Q26;
            {var subQ1=sQuery(id+"F2.wireOp",EDGE,"E12.23.1");Q26=makeQuery(id+"F2.imprint","IMPRINT",FACE,{"disambiguationData":[TD([[makeQuery(id+"F2.imprint","IMPRINT",EDGE,{"derivedFrom":subQ1}),1.0]])]});}
            var Q27;
            {var subQ0=sQuery(id+"F2.wireOp",EDGE,"E13");var subQ1=sQuery(id+"F2.wireOp",EDGE,"E12.23.2");var subQ2=makeQuery(id+"F2.imprint","INTERSECT",VERTEX,{"derivedFrom":[subQ1,subQ0]});Q27=makeQuery(id+"F2.imprint","IMPRINT",FACE,{"disambiguationData":[TD([[makeQuery(id+"F2.imprint","IMPRINT",EDGE,{"disambiguationData":[TD([[subQ2,1.0]])],"derivedFrom":subQ1}),-1.0]])]});}
            var Q28;
            {var subQ0=sQuery(id+"F2.wireOp",EDGE,"E13");var subQ1=sQuery(id+"F2.wireOp",EDGE,"E12.21.0");var subQ2=makeQuery(id+"F2.imprint","INTERSECT",VERTEX,{"derivedFrom":[subQ1,subQ0]});Q28=makeQuery(id+"F2.imprint","IMPRINT",FACE,{"disambiguationData":[TD([[makeQuery(id+"F2.imprint","IMPRINT",EDGE,{"disambiguationData":[TD([[subQ2,-1.0]])],"derivedFrom":subQ1}),-1.0]])]});}
            var Q29;
            {var subQ1=sQuery(id+"F2.wireOp",EDGE,"E12.21.1");Q29=makeQuery(id+"F2.imprint","IMPRINT",FACE,{"disambiguationData":[TD([[makeQuery(id+"F2.imprint","IMPRINT",EDGE,{"derivedFrom":subQ1}),1.0]])]});}
            var Q30;
            {var subQ8=sQuery(id+"F2.wireOp",EDGE,"E12.19.1");Q30=makeQuery(id+"F2.imprint","IMPRINT",FACE,{"disambiguationData":[TD([[makeQuery(id+"F2.imprint","IMPRINT",EDGE,{"derivedFrom":subQ8}),1.0]])]});}
            var Q31;
            {var subQ0=sQuery(id+"F2.wireOp",EDGE,"E13");var subQ1=sQuery(id+"F2.wireOp",EDGE,"E12.19.2");var subQ2=makeQuery(id+"F2.imprint","INTERSECT",VERTEX,{"derivedFrom":[subQ1,subQ0]});Q31=makeQuery(id+"F2.imprint","IMPRINT",FACE,{"disambiguationData":[TD([[makeQuery(id+"F2.imprint","IMPRINT",EDGE,{"disambiguationData":[TD([[subQ2,1.0]])],"derivedFrom":subQ1}),-1.0]])]});}
            var Q32;
            {var subQ0=sQuery(id+"F2.wireOp",EDGE,"E13");var subQ1=sQuery(id+"F2.wireOp",EDGE,"E12.21.2");var subQ2=makeQuery(id+"F2.imprint","INTERSECT",VERTEX,{"derivedFrom":[subQ1,subQ0]});Q32=makeQuery(id+"F2.imprint","IMPRINT",FACE,{"disambiguationData":[TD([[makeQuery(id+"F2.imprint","IMPRINT",EDGE,{"disambiguationData":[TD([[subQ2,1.0]])],"derivedFrom":subQ1}),-1.0]])]});}
            var Q33;
            {var subQ0=sQuery(id+"F2.wireOp",EDGE,"E13");var subQ1=sQuery(id+"F2.wireOp",EDGE,"E12.17.0");var subQ2=makeQuery(id+"F2.imprint","INTERSECT",VERTEX,{"derivedFrom":[subQ1,subQ0]});Q33=makeQuery(id+"F2.imprint","IMPRINT",FACE,{"disambiguationData":[TD([[makeQuery(id+"F2.imprint","IMPRINT",EDGE,{"disambiguationData":[TD([[subQ2,-1.0]])],"derivedFrom":subQ1}),-1.0]])]});}
            var Q34;
            {var subQ6=sQuery(id+"F2.wireOp",EDGE,"E12.17.1");Q34=makeQuery(id+"F2.imprint","IMPRINT",FACE,{"disambiguationData":[TD([[makeQuery(id+"F2.imprint","IMPRINT",EDGE,{"derivedFrom":subQ6}),1.0]])]});}
            var Q35;
            {var subQ0=sQuery(id+"F2.wireOp",EDGE,"E13");var subQ1=sQuery(id+"F2.wireOp",EDGE,"E12.17.2");var subQ2=makeQuery(id+"F2.imprint","INTERSECT",VERTEX,{"derivedFrom":[subQ1,subQ0]});Q35=makeQuery(id+"F2.imprint","IMPRINT",FACE,{"disambiguationData":[TD([[makeQuery(id+"F2.imprint","IMPRINT",EDGE,{"disambiguationData":[TD([[subQ2,1.0]])],"derivedFrom":subQ1}),-1.0]])]});}
            var Q36;
            {var subQ0=sQuery(id+"F2.wireOp",EDGE,"E13");var subQ1=sQuery(id+"F2.wireOp",EDGE,"E12.15.0");var subQ2=makeQuery(id+"F2.imprint","INTERSECT",VERTEX,{"derivedFrom":[subQ1,subQ0]});Q36=makeQuery(id+"F2.imprint","IMPRINT",FACE,{"disambiguationData":[TD([[makeQuery(id+"F2.imprint","IMPRINT",EDGE,{"disambiguationData":[TD([[subQ2,-1.0]])],"derivedFrom":subQ1}),-1.0]])]});}
            var Q37;
            {var subQ5=sQuery(id+"F2.wireOp",EDGE,"E12.15.1");Q37=makeQuery(id+"F2.imprint","IMPRINT",FACE,{"disambiguationData":[TD([[makeQuery(id+"F2.imprint","IMPRINT",EDGE,{"derivedFrom":subQ5}),1.0]])]});}
            var Q38;
            {var subQ0=sQuery(id+"F2.wireOp",EDGE,"E13");var subQ1=sQuery(id+"F2.wireOp",EDGE,"E12.15.2");var subQ2=makeQuery(id+"F2.imprint","INTERSECT",VERTEX,{"derivedFrom":[subQ1,subQ0]});Q38=makeQuery(id+"F2.imprint","IMPRINT",FACE,{"disambiguationData":[TD([[makeQuery(id+"F2.imprint","IMPRINT",EDGE,{"disambiguationData":[TD([[subQ2,1.0]])],"derivedFrom":subQ1}),-1.0]])]});}
            var Q39;
            {var subQ0=sQuery(id+"F2.wireOp",EDGE,"E13");var subQ1=sQuery(id+"F2.wireOp",EDGE,"E12.13.0");var subQ2=makeQuery(id+"F2.imprint","INTERSECT",VERTEX,{"derivedFrom":[subQ1,subQ0]});Q39=makeQuery(id+"F2.imprint","IMPRINT",FACE,{"disambiguationData":[TD([[makeQuery(id+"F2.imprint","IMPRINT",EDGE,{"disambiguationData":[TD([[subQ2,-1.0]])],"derivedFrom":subQ1}),-1.0]])]});}
            var Q40;
            {var subQ1=sQuery(id+"F2.wireOp",EDGE,"E12.13.1");Q40=makeQuery(id+"F2.imprint","IMPRINT",FACE,{"disambiguationData":[TD([[makeQuery(id+"F2.imprint","IMPRINT",EDGE,{"derivedFrom":subQ1}),1.0]])]});}
            var Q41;
            {var subQ0=sQuery(id+"F2.wireOp",EDGE,"E13");var subQ1=sQuery(id+"F2.wireOp",EDGE,"E12.13.2");var subQ2=makeQuery(id+"F2.imprint","INTERSECT",VERTEX,{"derivedFrom":[subQ1,subQ0]});Q41=makeQuery(id+"F2.imprint","IMPRINT",FACE,{"disambiguationData":[TD([[makeQuery(id+"F2.imprint","IMPRINT",EDGE,{"disambiguationData":[TD([[subQ2,1.0]])],"derivedFrom":subQ1}),-1.0]])]});}
            var Q42;
            {var subQ0=sQuery(id+"F2.wireOp",EDGE,"E13");var subQ1=sQuery(id+"F2.wireOp",EDGE,"E12.11.0");var subQ2=makeQuery(id+"F2.imprint","INTERSECT",VERTEX,{"derivedFrom":[subQ1,subQ0]});Q42=makeQuery(id+"F2.imprint","IMPRINT",FACE,{"disambiguationData":[TD([[makeQuery(id+"F2.imprint","IMPRINT",EDGE,{"disambiguationData":[TD([[subQ2,-1.0]])],"derivedFrom":subQ1}),-1.0]])]});}
            var Q43;
            {var subQ1=sQuery(id+"F2.wireOp",EDGE,"E12.11.1");Q43=makeQuery(id+"F2.imprint","IMPRINT",FACE,{"disambiguationData":[TD([[makeQuery(id+"F2.imprint","IMPRINT",EDGE,{"derivedFrom":subQ1}),1.0]])]});}
            var Q44;
            {var subQ0=sQuery(id+"F2.wireOp",EDGE,"E13");var subQ1=sQuery(id+"F2.wireOp",EDGE,"E12.11.2");var subQ2=makeQuery(id+"F2.imprint","INTERSECT",VERTEX,{"derivedFrom":[subQ1,subQ0]});Q44=makeQuery(id+"F2.imprint","IMPRINT",FACE,{"disambiguationData":[TD([[makeQuery(id+"F2.imprint","IMPRINT",EDGE,{"disambiguationData":[TD([[subQ2,1.0]])],"derivedFrom":subQ1}),-1.0]])]});}
            var Q45;
            {var subQ0=sQuery(id+"F2.wireOp",EDGE,"E13");var subQ1=sQuery(id+"F2.wireOp",EDGE,"E12.9.0");var subQ2=makeQuery(id+"F2.imprint","INTERSECT",VERTEX,{"derivedFrom":[subQ1,subQ0]});Q45=makeQuery(id+"F2.imprint","IMPRINT",FACE,{"disambiguationData":[TD([[makeQuery(id+"F2.imprint","IMPRINT",EDGE,{"disambiguationData":[TD([[subQ2,-1.0]])],"derivedFrom":subQ1}),-1.0]])]});}
            var Q46;
            {var subQ0=sQuery(id+"F2.wireOp",EDGE,"E13");var subQ1=sQuery(id+"F2.wireOp",EDGE,"E12.9.2");var subQ2=makeQuery(id+"F2.imprint","INTERSECT",VERTEX,{"derivedFrom":[subQ1,subQ0]});Q46=makeQuery(id+"F2.imprint","IMPRINT",FACE,{"disambiguationData":[TD([[makeQuery(id+"F2.imprint","IMPRINT",EDGE,{"disambiguationData":[TD([[subQ2,1.0]])],"derivedFrom":subQ1}),-1.0]])]});}
            var Q47;
            {var subQ6=sQuery(id+"F2.wireOp",EDGE,"E12.9.1");Q47=makeQuery(id+"F2.imprint","IMPRINT",FACE,{"disambiguationData":[TD([[makeQuery(id+"F2.imprint","IMPRINT",EDGE,{"derivedFrom":subQ6}),1.0]])]});}
            var Q48;
            {var subQ0=sQuery(id+"F2.wireOp",EDGE,"E13");var subQ1=sQuery(id+"F2.wireOp",EDGE,"E12.7.0");var subQ2=makeQuery(id+"F2.imprint","INTERSECT",VERTEX,{"derivedFrom":[subQ1,subQ0]});Q48=makeQuery(id+"F2.imprint","IMPRINT",FACE,{"disambiguationData":[TD([[makeQuery(id+"F2.imprint","IMPRINT",EDGE,{"disambiguationData":[TD([[subQ2,-1.0]])],"derivedFrom":subQ1}),-1.0]])]});}
            var Q49;
            {var subQ1=sQuery(id+"F2.wireOp",EDGE,"E12.7.1");Q49=makeQuery(id+"F2.imprint","IMPRINT",FACE,{"disambiguationData":[TD([[makeQuery(id+"F2.imprint","IMPRINT",EDGE,{"derivedFrom":subQ1}),1.0]])]});}
            var Q50;
            {var subQ0=sQuery(id+"F2.wireOp",EDGE,"E13");var subQ1=sQuery(id+"F2.wireOp",EDGE,"E12.6.0");var subQ2=makeQuery(id+"F2.imprint","INTERSECT",VERTEX,{"derivedFrom":[subQ1,subQ0]});Q50=makeQuery(id+"F2.imprint","IMPRINT",FACE,{"disambiguationData":[TD([[makeQuery(id+"F2.imprint","IMPRINT",EDGE,{"disambiguationData":[TD([[subQ2,-1.0]])],"derivedFrom":subQ1}),-1.0]])]});}
            var Q51;
            {var subQ0=sQuery(id+"F2.wireOp",EDGE,"E13");var subQ1=sQuery(id+"F2.wireOp",EDGE,"E12.5.0");var subQ2=makeQuery(id+"F2.imprint","INTERSECT",VERTEX,{"derivedFrom":[subQ1,subQ0]});Q51=makeQuery(id+"F2.imprint","IMPRINT",FACE,{"disambiguationData":[TD([[makeQuery(id+"F2.imprint","IMPRINT",EDGE,{"disambiguationData":[TD([[subQ2,-1.0]])],"derivedFrom":subQ1}),-1.0]])]});}
            var Q52;
            {var subQ6=sQuery(id+"F2.wireOp",EDGE,"E12.5.1");Q52=makeQuery(id+"F2.imprint","IMPRINT",FACE,{"disambiguationData":[TD([[makeQuery(id+"F2.imprint","IMPRINT",EDGE,{"derivedFrom":subQ6}),1.0]])]});}
            var Q53;
            {var subQ0=sQuery(id+"F2.wireOp",EDGE,"E13");var subQ1=sQuery(id+"F2.wireOp",EDGE,"E12.5.2");var subQ2=makeQuery(id+"F2.imprint","INTERSECT",VERTEX,{"derivedFrom":[subQ1,subQ0]});Q53=makeQuery(id+"F2.imprint","IMPRINT",FACE,{"disambiguationData":[TD([[makeQuery(id+"F2.imprint","IMPRINT",EDGE,{"disambiguationData":[TD([[subQ2,1.0]])],"derivedFrom":subQ1}),-1.0]])]});}
            extrude(context, id + "F3", {"entities" : qUnion([Q0, Q1, Q2, Q3, Q4, Q5, Q6, Q7, Q8, Q9, Q10, Q11, Q12, Q13, Q14, Q15, Q16, Q17, Q18, Q19, Q20, Q21, Q22, Q23, Q24, Q25, Q26, Q27, Q28, Q29, Q30, Q31, Q32, Q33, Q34, Q35, Q36, Q37, Q38, Q39, Q40, Q41, Q42, Q43, Q44, Q45, Q46, Q47, Q48, Q49, Q50, Q51, Q52, Q53]), "depth" : 3.5 * mm, "offsetDistance" : 25.4 * mm});
        }
        {
            var Q0;
            Q0=makeQuery(id+"F1.opExtrude","CAP_FACE",FACE,{"disambiguationData":[OSD([sQuery(id+"F0.wireOp",EDGE,"E0"),sQuery(id+"F0.wireOp",EDGE,"E1"),sQuery(id+"F0.wireOp",EDGE,"E3"),sQuery(id+"F0.wireOp",EDGE,"E5"),sQuery(id+"F0.wireOp",EDGE,"E6"),sQuery(id+"F0.wireOp",EDGE,"E7.1.0"),sQuery(id+"F0.wireOp",EDGE,"E7.1.1"),sQuery(id+"F0.wireOp",EDGE,"E7.1.2"),sQuery(id+"F0.wireOp",EDGE,"E7.2.0"),sQuery(id+"F0.wireOp",EDGE,"E7.2.1"),sQuery(id+"F0.wireOp",EDGE,"E7.2.2"),sQuery(id+"F0.wireOp",EDGE,"E7.3.0"),sQuery(id+"F0.wireOp",EDGE,"E7.3.1"),sQuery(id+"F0.wireOp",EDGE,"E7.3.2"),sQuery(id+"F0.wireOp",EDGE,"E7.4.0"),sQuery(id+"F0.wireOp",EDGE,"E7.4.1"),sQuery(id+"F0.wireOp",EDGE,"E7.4.2"),sQuery(id+"F0.wireOp",EDGE,"E7.5.0"),sQuery(id+"F0.wireOp",EDGE,"E7.5.1"),sQuery(id+"F0.wireOp",EDGE,"E7.5.2"),sQuery(id+"F0.wireOp",EDGE,"E7.6.0"),sQuery(id+"F0.wireOp",EDGE,"E7.6.1"),sQuery(id+"F0.wireOp",EDGE,"E7.6.2"),sQuery(id+"F0.wireOp",EDGE,"E7.7.0"),sQuery(id+"F0.wireOp",EDGE,"E7.7.1"),sQuery(id+"F0.wireOp",EDGE,"E7.7.2"),sQuery(id+"F0.wireOp",EDGE,"E7.8.0"),sQuery(id+"F0.wireOp",EDGE,"E7.8.1"),sQuery(id+"F0.wireOp",EDGE,"E7.8.2"),sQuery(id+"F0.wireOp",EDGE,"E7.9.0"),sQuery(id+"F0.wireOp",EDGE,"E7.9.1"),sQuery(id+"F0.wireOp",EDGE,"E7.9.2"),sQuery(id+"F0.wireOp",EDGE,"E7.10.0"),sQuery(id+"F0.wireOp",EDGE,"E7.10.1"),sQuery(id+"F0.wireOp",EDGE,"E7.10.2"),sQuery(id+"F0.wireOp",EDGE,"E7.11.0"),sQuery(id+"F0.wireOp",EDGE,"E7.11.1"),sQuery(id+"F0.wireOp",EDGE,"E7.11.2"),sQuery(id+"F0.wireOp",EDGE,"E7.12.0"),sQuery(id+"F0.wireOp",EDGE,"E7.12.1"),sQuery(id+"F0.wireOp",EDGE,"E7.12.2"),sQuery(id+"F0.wireOp",EDGE,"E7.13.0"),sQuery(id+"F0.wireOp",EDGE,"E7.13.1"),sQuery(id+"F0.wireOp",EDGE,"E7.13.2"),sQuery(id+"F0.wireOp",EDGE,"E7.14.0"),sQuery(id+"F0.wireOp",EDGE,"E7.14.1"),sQuery(id+"F0.wireOp",EDGE,"E7.14.2"),sQuery(id+"F0.wireOp",EDGE,"E7.15.0"),sQuery(id+"F0.wireOp",EDGE,"E7.15.1"),sQuery(id+"F0.wireOp",EDGE,"E7.15.2"),sQuery(id+"F0.wireOp",EDGE,"E7.16.0"),sQuery(id+"F0.wireOp",EDGE,"E7.16.1"),sQuery(id+"F0.wireOp",EDGE,"E7.16.2"),sQuery(id+"F0.wireOp",EDGE,"E7.17.0"),sQuery(id+"F0.wireOp",EDGE,"E7.17.1"),sQuery(id+"F0.wireOp",EDGE,"E7.17.2")])],"isStart":false});
            var sketch = newSketch(context, id + "F4", { "sketchPlane" : qUnion([Q0])});
            skArc(sketch, "E14", {"start": v(9.85, 8.31) * mm, "mid": v(6.26, 14.34) * mm, "end": v(0, 17.5) * mm});
            skArc(sketch, "E15", {"start": v(9.85, 8.31) * mm, "mid": v(5.41, 11.64) * mm, "end": v(0, 12.83) * mm});
            skArc(sketch, "E16", {"start": v(0, 17.5) * mm, "mid": v(-2.29, 15.17) * mm, "end": v(0, 12.83) * mm});
            skArc(sketch, "E17.1.0", {"start": v(-16.65, 5.4) * mm, "mid": v(-15.13, 2.51) * mm, "end": v(-12.2, 3.96) * mm});
            skArc(sketch, "E17.1.1", {"start": v(-4.86, 11.94) * mm, "mid": v(-11.7, 10.39) * mm, "end": v(-16.65, 5.4) * mm});
            skArc(sketch, "E17.1.2", {"start": v(-4.86, 11.94) * mm, "mid": v(-9.4, 8.74) * mm, "end": v(-12.2, 3.96) * mm});
            skArc(sketch, "E17.2.0", {"start": v(-10.29, -14.16) * mm, "mid": v(-7.07, -13.61) * mm, "end": v(-7.54, -10.38) * mm});
            skArc(sketch, "E17.2.1", {"start": v(-12.85, -0.94) * mm, "mid": v(-13.5, -7.92) * mm, "end": v(-10.29, -14.16) * mm});
            skArc(sketch, "E17.2.2", {"start": v(-12.85, -0.94) * mm, "mid": v(-11.22, -6.23) * mm, "end": v(-7.54, -10.38) * mm});
            skArc(sketch, "E17.3.0", {"start": v(10.29, -14.16) * mm, "mid": v(10.76, -10.93) * mm, "end": v(7.54, -10.38) * mm});
            skArc(sketch, "E17.3.1", {"start": v(-3.08, -12.51) * mm, "mid": v(3.36, -15.28) * mm, "end": v(10.29, -14.16) * mm});
            skArc(sketch, "E17.3.2", {"start": v(-3.08, -12.51) * mm, "mid": v(2.46, -12.6) * mm, "end": v(7.54, -10.38) * mm});
            skArc(sketch, "E17.4.0", {"start": v(16.65, 5.4) * mm, "mid": v(13.72, 6.86) * mm, "end": v(12.2, 3.96) * mm});
            skArc(sketch, "E17.4.1", {"start": v(10.95, -6.8) * mm, "mid": v(15.58, -1.52) * mm, "end": v(16.65, 5.4) * mm});
            skArc(sketch, "E17.4.2", {"start": v(10.95, -6.8) * mm, "mid": v(12.74, -1.55) * mm, "end": v(12.2, 3.96) * mm});
            skPoint(sketch, "E17.center", {"position": v(0, 0) * mm});
            skSolve(sketch);
        }
        {
            var Q0;
            Q0=makeQuery(id+"F4.imprint","IMPRINT",FACE,{"disambiguationData":[TD([[makeQuery(id+"F4.imprint","IMPRINT",EDGE,{"derivedFrom":sQuery(id+"F4.wireOp",EDGE,"E17.1.0")}),1.0]])]});
            var Q1;
            Q1=makeQuery(id+"F4.imprint","IMPRINT",FACE,{"disambiguationData":[TD([[makeQuery(id+"F4.imprint","IMPRINT",EDGE,{"derivedFrom":sQuery(id+"F4.wireOp",EDGE,"E14")}),1.0]])]});
            var Q2;
            Q2=makeQuery(id+"F4.imprint","IMPRINT",FACE,{"disambiguationData":[TD([[makeQuery(id+"F4.imprint","IMPRINT",EDGE,{"derivedFrom":sQuery(id+"F4.wireOp",EDGE,"E17.4.0")}),1.0]])]});
            var Q3;
            Q3=makeQuery(id+"F4.imprint","IMPRINT",FACE,{"disambiguationData":[TD([[makeQuery(id+"F4.imprint","IMPRINT",EDGE,{"derivedFrom":sQuery(id+"F4.wireOp",EDGE,"E17.3.0")}),1.0]])]});
            var Q4;
            Q4=makeQuery(id+"F4.imprint","IMPRINT",FACE,{"disambiguationData":[TD([[makeQuery(id+"F4.imprint","IMPRINT",EDGE,{"derivedFrom":sQuery(id+"F4.wireOp",EDGE,"E17.2.0")}),1.0]])]});
            extrude(context, id + "F5", {"entities" : qUnion([Q0, Q1, Q2, Q3, Q4]), "operationType" : NewBodyOperationType.REMOVE, "oppositeDirection" : true, "depth" : 25.4 * mm, "offsetDistance" : 25.4 * mm});
        }
    });
